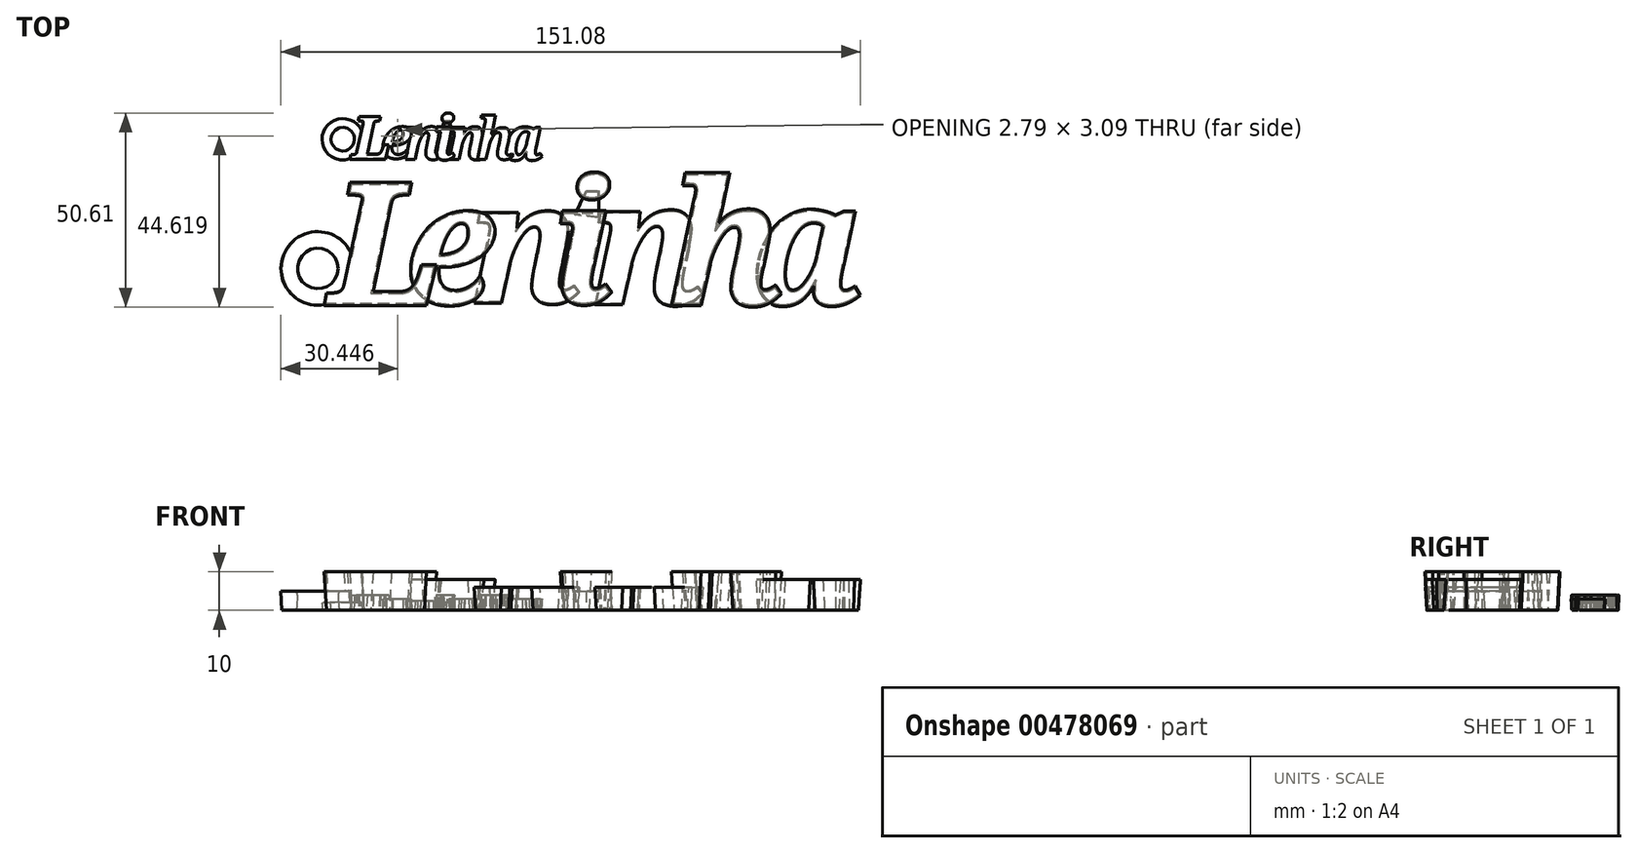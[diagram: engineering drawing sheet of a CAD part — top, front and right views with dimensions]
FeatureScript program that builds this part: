
annotation { "Feature Type Name" : "Feature", "Feature Type Description" : "" }
export const myFeature = defineFeature(function(context is Context, id is Id, definition is map)
    precondition{}
    {
        {
            var Q0;
            Q0=qCreatedBy(makeId("Top.planeOp"),FACE);
            var sketch = newSketch(context, id + "F0", { "sketchPlane" : qUnion([Q0])});
            skText(sketch, "E0", { "text": "L", "fontName": "NotoSerif-BoldItalic.ttf"});
            const initialGuessF0  = {"E0": [-0.05207, -0.02728, 1, 0, 0.01084]};
            skSetInitialGuess(sketch, initialGuessF0);
            skSolve(sketch);
        }
        {
            var Q0;
            Q0=qCreatedBy(makeId("Top.planeOp"),FACE);
            var sketch = newSketch(context, id + "F1", { "sketchPlane" : qUnion([Q0])});
            skText(sketch, "E1", { "text": "e", "fontName": "NotoSerif-BoldItalic.ttf"});
            const initialGuessF1  = {"E1": [-0.04471, -0.02723, 1, 0, 0.01093]};
            skSetInitialGuess(sketch, initialGuessF1);
            skSolve(sketch);
        }
        {
            var Q0;
            Q0=qCreatedBy(makeId("Top.planeOp"),FACE);
            var sketch = newSketch(context, id + "F2", { "sketchPlane" : qUnion([Q0])});
            skText(sketch, "E2", { "text": "n", "fontName": "NotoSerif-BoldItalic.ttf"});
            const initialGuessF2  = {"E2": [-0.03864, -0.02735, 1, 0, 0.01093]};
            skSetInitialGuess(sketch, initialGuessF2);
            skSolve(sketch);
        }
        {
            var Q0;
            Q0=qCreatedBy(makeId("Top.planeOp"),FACE);
            var sketch = newSketch(context, id + "F3", { "sketchPlane" : qUnion([Q0])});
            skText(sketch, "E3", { "text": "i", "fontName": "NotoSerif-BoldItalic.ttf"});
            const initialGuessF3  = {"E3": [-0.03088, -0.0274, 1, 0, 0.01102]};
            skSetInitialGuess(sketch, initialGuessF3);
            skSolve(sketch);
        }
        {
            var Q0;
            Q0=qCreatedBy(makeId("Top.planeOp"),FACE);
            var sketch = newSketch(context, id + "F4", { "sketchPlane" : qUnion([Q0])});
            skText(sketch, "E4", { "text": "n", "fontName": "NotoSerif-BoldItalic.ttf"});
            const initialGuessF4  = {"E4": [-0.02727, -0.0274, 1, 0, 0.01093]};
            skSetInitialGuess(sketch, initialGuessF4);
            skSolve(sketch);
        }
        {
            var Q0;
            Q0=qCreatedBy(makeId("Top.planeOp"),FACE);
            var sketch = newSketch(context, id + "F5", { "sketchPlane" : qUnion([Q0])});
            skText(sketch, "E5", { "text": "h", "fontName": "NotoSerif-BoldItalic.ttf"});
            const initialGuessF5  = {"E5": [-0.0198, -0.02746, 1, 0, 0.01088]};
            skSetInitialGuess(sketch, initialGuessF5);
            skSolve(sketch);
        }
        {
            var Q0;
            Q0=qCreatedBy(makeId("Top.planeOp"),FACE);
            var sketch = newSketch(context, id + "F6", { "sketchPlane" : qUnion([Q0])});
            skText(sketch, "E6", { "text": "a", "fontName": "NotoSerif-BoldItalic.ttf"});
            const initialGuessF6  = {"E6": [-0.0125, -0.02753, 1, 0, 0.01107]};
            skSetInitialGuess(sketch, initialGuessF6);
            skSolve(sketch);
        }
        {
            var Q0;
            Q0 = qSketchRegion(id + "F0", true);
            extrude(context, id + "F7", {"entities" : qUnion([Q0]), "depth" : 4 * mm, "hasDraft" : true, "draftAngle" : 3 * degree});
        }
        {
            var Q0;
            Q0 = qSketchRegion(id + "F1", true);
            extrude(context, id + "F8", {"entities" : qUnion([Q0]), "operationType" : NewBodyOperationType.ADD, "depth" : 3 * mm});
        }
        {
            var Q0;
            Q0 = qSketchRegion(id + "F2", true);
            extrude(context, id + "F9", {"entities" : qUnion([Q0]), "operationType" : NewBodyOperationType.ADD, "depth" : 2.5 * mm, "hasDraft" : true, "draftAngle" : 3 * degree});
        }
        {
            var Q0;
            Q0 = qSketchRegion(id + "F3", true);
            extrude(context, id + "F10", {"entities" : qUnion([Q0]), "operationType" : NewBodyOperationType.ADD, "depth" : 4 * mm, "hasDraft" : true, "draftAngle" : 3 * degree});
        }
        {
            var Q0;
            Q0 = qSketchRegion(id + "F4", true);
            extrude(context, id + "F11", {"entities" : qUnion([Q0]), "operationType" : NewBodyOperationType.ADD, "depth" : 3 * mm, "hasDraft" : true, "draftAngle" : 3 * degree});
        }
        {
            var Q0;
            Q0=makeQuery(id+"F5.imprint","IMPRINT",FACE,{"disambiguationData":[TD([[makeQuery(id+"F5.imprint","IMPRINT",EDGE,{"derivedFrom":sQuery(id+"F5.wireOp",EDGE,"E5.sketch_text.stroke-0")}),-1.0]])]});
            extrude(context, id + "F12", {"entities" : qUnion([Q0]), "operationType" : NewBodyOperationType.ADD, "depth" : 4 * mm});
        }
        {
            var Q0;
            Q0 = qSketchRegion(id + "F6", true);
            extrude(context, id + "F13", {"entities" : qUnion([Q0]), "operationType" : NewBodyOperationType.ADD, "depth" : 3 * mm, "hasDraft" : true, "draftAngle" : 3 * degree});
        }
        {
            var Q0;
            Q0=qCreatedBy(makeId("Top.planeOp"),FACE);
            cPlane(context, id + "F14", {"entities" : qUnion([Q0]), "cplaneType" : CPlaneType.OFFSET, "offset" : 2 * mm, "width" : 150 * mm, "height" : 150 * mm});
        }
        {
            var Q0;
            Q0=qCreatedBy(id+"F14.planeOp",FACE);
            var sketch = newSketch(context, id + "F15", { "sketchPlane" : qUnion([Q0])});
            skLineSegment(sketch, "E7", {"start": v(-28.6, -19.29) * mm, "end": v(-27.94, -17.56) * mm});
            skLineSegment(sketch, "E8", {"start": v(-27.94, -17.56) * mm, "end": v(-26.62, -17.56) * mm});
            skLineSegment(sketch, "E9", {"start": v(-26.62, -17.56) * mm, "end": v(-26.62, -19.54) * mm});
            skLineSegment(sketch, "E10", {"start": v(-26.62, -19.54) * mm, "end": v(-28.6, -19.29) * mm});
            skSolve(sketch);
        }
        {
            var Q0;
            Q0 = qSketchRegion(id + "F15", true);
            extrude(context, id + "F16", {"entities" : qUnion([Q0]), "oppositeDirection" : true, "depth" : 1.99 * mm, "hasDraft" : true, "draftAngle" : 3 * degree, "hasSecondDirectionDraft" : true, "secondDirectionDraftAngle" : 3 * degree});
        }
        {
            var Q0;
            Q0=qCreatedBy(id+"F14.planeOp",FACE);
            var sketch = newSketch(context, id + "F17", { "sketchPlane" : qUnion([Q0])});
            skCircle(sketch, "E11", {"center": v(-54.58, -22.25) * mm, "radius": 5.31 * mm});
            skCircle(sketch, "E12", {"center": v(-54.58, -22.25) * mm, "radius": 3.16 * mm});
            skSolve(sketch);
        }
        {
            var Q0;
            Q0 = qSketchRegion(id + "F17", true);
            extrude(context, id + "F18", {"entities" : qUnion([Q0]), "operationType" : NewBodyOperationType.ADD, "oppositeDirection" : true, "depth" : 2 * mm, "hasDraft" : true, "draftAngle" : 3 * degree, "hasSecondDirectionDraft" : true, "secondDirectionDraftAngle" : 3 * degree});
        }
        {
            var Q0;
            Q0=makeQuery(id+"F18.opExtrude","CAP_EDGE",EDGE,{"disambiguationData":[OSD([sQuery(id+"F17.wireOp",EDGE,"E12")])],"isStart":false});
            var Q1;
            Q1=makeQuery(id+"F18.opExtrude","CAP_EDGE",EDGE,{"disambiguationData":[OSD([sQuery(id+"F17.wireOp",EDGE,"E12")])],"isStart":true});
            fillet(context, id + "F19", {"entities" : qUnion([Q0, Q1]), "radius" : .2 * mm, "tangentPropagation" : true, "allowEdgeOverflow" : false});
        }
        {
            var Q0;
            Q0=makeQuery(id+"F18.opExtrude","CAP_EDGE",EDGE,{"disambiguationData":[OSD([sQuery(id+"F17.wireOp",EDGE,"E11")])],"isStart":true});
            var Q1;
            Q1=makeQuery(id+"F18.opExtrude","CAP_EDGE",EDGE,{"disambiguationData":[OSD([sQuery(id+"F17.wireOp",EDGE,"E11")])],"isStart":false});
            fillet(context, id + "F20", {"entities" : qUnion([Q0, Q1]), "radius" : .3 * mm, "tangentPropagation" : true, "allowEdgeOverflow" : false});
        }
        {
            var Q0;
            Q0=qCreatedBy(makeId("Top.planeOp"),FACE);
            var sketch = newSketch(context, id + "F21", { "sketchPlane" : qUnion([Q0])});
            skText(sketch, "E13", { "text": "L", "fontName": "NotoSerif-BoldItalic.ttf"});
            const initialGuessF21  = {"E13": [-0.05779, -0.06515, 1, 0, 0.03141]};
            skSetInitialGuess(sketch, initialGuessF21);
            skSolve(sketch);
        }
        {
            var Q0;
            Q0=qCreatedBy(makeId("Top.planeOp"),FACE);
            var sketch = newSketch(context, id + "F22", { "sketchPlane" : qUnion([Q0])});
            skText(sketch, "E14", { "text": "e", "fontName": "NotoSerif-BoldItalic.ttf"});
            const initialGuessF22  = {"E14": [-0.03821, -0.0649, 1, 0, 0.03117]};
            skSetInitialGuess(sketch, initialGuessF22);
            skSolve(sketch);
        }
        {
            var Q0;
            Q0=qCreatedBy(makeId("Top.planeOp"),FACE);
            var sketch = newSketch(context, id + "F23", { "sketchPlane" : qUnion([Q0])});
            skText(sketch, "E15", { "text": "n", "fontName": "NotoSerif-BoldItalic.ttf"});
            const initialGuessF23  = {"E15": [-0.0215, -0.06466, 1, 0, 0.03095]};
            skSetInitialGuess(sketch, initialGuessF23);
            skSolve(sketch);
        }
        {
            var Q0;
            Q0=qCreatedBy(makeId("Top.planeOp"),FACE);
            var sketch = newSketch(context, id + "F24", { "sketchPlane" : qUnion([Q0])});
            skText(sketch, "E16", { "text": "i", "fontName": "NotoSerif-BoldItalic.ttf"});
            const initialGuessF24  = {"E16": [0.00027, -0.06465, 1, 0, 0.03117]};
            skSetInitialGuess(sketch, initialGuessF24);
            skSolve(sketch);
        }
        {
            var Q0;
            Q0=qCreatedBy(makeId("Top.planeOp"),FACE);
            var sketch = newSketch(context, id + "F25", { "sketchPlane" : qUnion([Q0])});
            skText(sketch, "E17", { "text": "n", "fontName": "NotoSerif-BoldItalic.ttf"});
            const initialGuessF25  = {"E17": [0.00995, -0.06508, 1, 0, 0.03183]};
            skSetInitialGuess(sketch, initialGuessF25);
            skSolve(sketch);
        }
        {
            var Q0;
            Q0=qCreatedBy(makeId("Top.planeOp"),FACE);
            var sketch = newSketch(context, id + "F26", { "sketchPlane" : qUnion([Q0])});
            skText(sketch, "E18", { "text": "h", "fontName": "NotoSerif-BoldItalic.ttf"});
            const initialGuessF26  = {"E18": [0.03085, -0.06506, 1, 0, 0.03183]};
            skSetInitialGuess(sketch, initialGuessF26);
            skSolve(sketch);
        }
        {
            var Q0;
            Q0=qCreatedBy(makeId("Top.planeOp"),FACE);
            var sketch = newSketch(context, id + "F27", { "sketchPlane" : qUnion([Q0])});
            skText(sketch, "E19", { "text": "a", "fontName": "NotoSerif-BoldItalic.ttf"});
            const initialGuessF27  = {"E19": [0.05196, -0.06504, 1, 0, 0.03183]};
            skSetInitialGuess(sketch, initialGuessF27);
            skSolve(sketch);
        }
        {
            var Q0;
            Q0=qCreatedBy(makeId("Top.planeOp"),FACE);
            var sketch = newSketch(context, id + "F28", { "sketchPlane" : qUnion([Q0])});
            skCircle(sketch, "E20", {"center": v(-61.09, -55.93) * mm, "radius": 9.34 * mm});
            skCircle(sketch, "E21", {"center": v(-61.09, -55.93) * mm, "radius": 5.5 * mm});
            skSolve(sketch);
        }
        {
            var Q0;
            Q0=makeQuery(id+"F21.imprint","IMPRINT",FACE,{"disambiguationData":[TD([[makeQuery(id+"F21.imprint","IMPRINT",EDGE,{"derivedFrom":sQuery(id+"F21.wireOp",EDGE,"E13.sketch_text.stroke-0")}),-1.0]])]});
            var Q1;
            Q1 = qSketchRegion(id + "F24", true);
            var Q2;
            Q2 = qSketchRegion(id + "F26", true);
            extrude(context, id + "F29", {"entities" : qUnion([Q0, Q1, Q2]), "depth" : 10 * mm, "hasDraft" : true, "draftAngle" : 3 * degree});
        }
        {
            var Q0;
            Q0 = qSketchRegion(id + "F23", true);
            var Q1;
            Q1 = qSketchRegion(id + "F25", true);
            extrude(context, id + "F30", {"entities" : qUnion([Q0, Q1]), "depth" : 6 * mm, "hasDraft" : true, "draftAngle" : 3 * degree});
        }
        {
            var Q0;
            Q0 = qSketchRegion(id + "F22", true);
            var Q1;
            Q1 = qSketchRegion(id + "F27", true);
            extrude(context, id + "F31", {"entities" : qUnion([Q0, Q1]), "depth" : 8 * mm, "hasDraft" : true, "draftAngle" : 3 * degree});
        }
        {
            var Q0;
            Q0=makeQuery(id+"F28.imprint","IMPRINT",FACE,{"disambiguationData":[TD([[makeQuery(id+"F28.imprint","IMPRINT",EDGE,{"derivedFrom":sQuery(id+"F28.wireOp",EDGE,"E20")}),1.0]])]});
            extrude(context, id + "F32", {"entities" : qUnion([Q0]), "operationType" : NewBodyOperationType.ADD, "depth" : 5 * mm, "hasDraft" : true, "draftAngle" : 3 * degree});
        }
        {
            var Q0;
            Q0=qCreatedBy(makeId("Top.planeOp"),FACE);
            var sketch = newSketch(context, id + "F33", { "sketchPlane" : qUnion([Q0])});
            skLineSegment(sketch, "E22", {"start": v(6.4, -41.82) * mm, "end": v(9, -35.94) * mm});
            skLineSegment(sketch, "E23", {"start": v(9, -35.94) * mm, "end": v(11.88, -35.94) * mm});
            skLineSegment(sketch, "E24", {"start": v(11.88, -35.94) * mm, "end": v(11.88, -42.48) * mm});
            skLineSegment(sketch, "E25", {"start": v(11.88, -42.48) * mm, "end": v(6.4, -41.82) * mm});
            skSolve(sketch);
        }
        {
            var Q0;
            Q0 = qSketchRegion(id + "F33", true);
            extrude(context, id + "F34", {"entities" : qUnion([Q0]), "depth" : 5 * mm, "hasDraft" : true, "draftAngle" : 3 * degree});
        }
        {
            var Q0;
            Q0=makeQuery(id+"F32.opExtrude","CAP_EDGE",EDGE,{"disambiguationData":[OSD([sQuery(id+"F28.wireOp",EDGE,"E21")])],"isStart":false});
            var Q1;
            Q1=makeQuery(id+"F32.opExtrude","CAP_EDGE",EDGE,{"disambiguationData":[OSD([sQuery(id+"F28.wireOp",EDGE,"E21")])],"isStart":true});
            fillet(context, id + "F35", {"entities" : qUnion([Q0, Q1]), "radius" : 1 * mm, "tangentPropagation" : true, "allowEdgeOverflow" : false});
        }
    });
